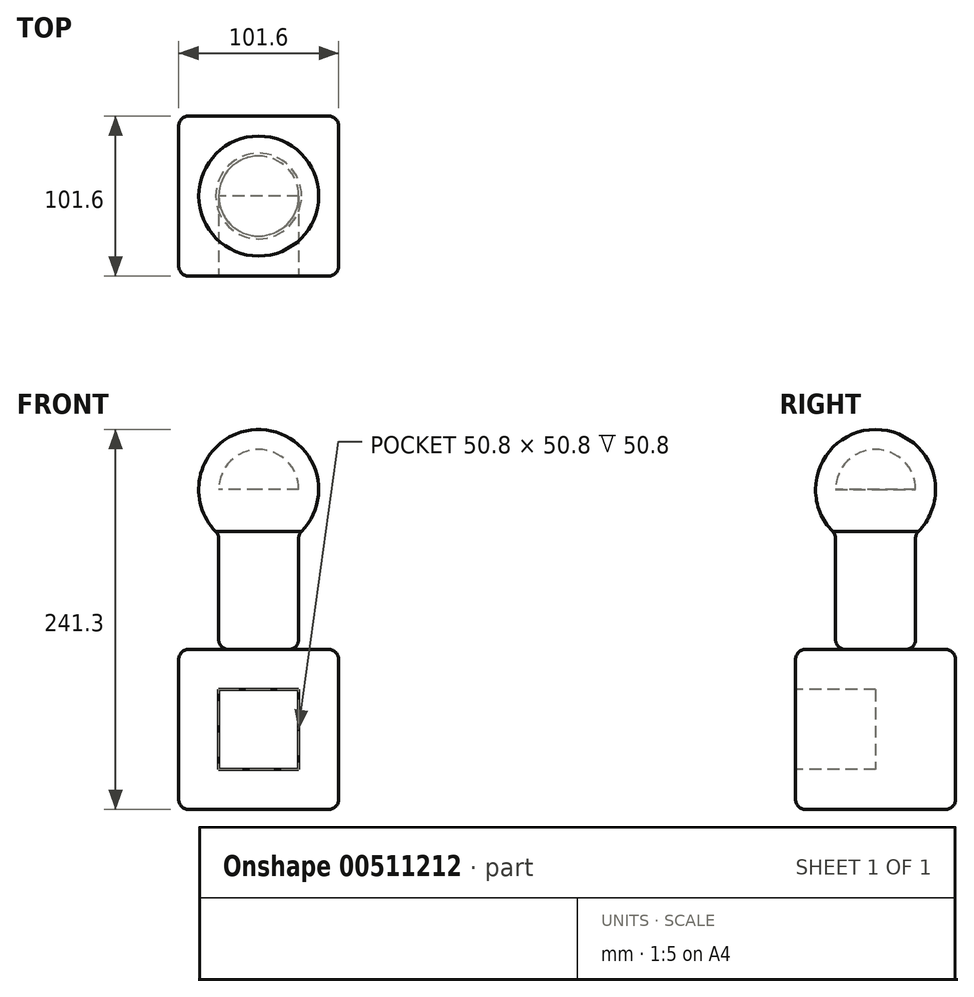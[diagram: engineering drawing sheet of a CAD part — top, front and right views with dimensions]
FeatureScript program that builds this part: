
annotation { "Feature Type Name" : "Feature", "Feature Type Description" : "" }
export const myFeature = defineFeature(function(context is Context, id is Id, definition is map)
    precondition{}
    {
        {
            var Q0;
            Q0=qCreatedBy(makeId("Top.planeOp"),FACE);
            var sketch = newSketch(context, id + "F0", { "sketchPlane" : qUnion([Q0])});
            skLineSegment(sketch, "E0.bottom", {"start": v(50.8, 50.8) * mm, "end": v(-50.8, 50.8) * mm});
            skLineSegment(sketch, "E0.top", {"start": v(50.8, -50.8) * mm, "end": v(-50.8, -50.8) * mm});
            skLineSegment(sketch, "E0.left", {"start": v(50.8, 50.8) * mm, "end": v(50.8, -50.8) * mm});
            skLineSegment(sketch, "E0.right", {"start": v(-50.8, 50.8) * mm, "end": v(-50.8, -50.8) * mm});
            skPoint(sketch, "E0.middle", {"position": v(0, 0) * mm});
            skSolve(sketch);
        }
        {
            var Q0;
            Q0=makeQuery(id+"F0.imprint","IMPRINT",FACE,{"disambiguationData":[TD([[makeQuery(id+"F0.imprint","IMPRINT",EDGE,{"derivedFrom":sQuery(id+"F0.wireOp",EDGE,"E0.bottom")}),1.0]])]});
            extrude(context, id + "F1", {"entities" : qUnion([Q0]), "depth" : 101.6 * mm});
        }
        {
            var Q0;
            Q0=makeQuery(id+"F1.opExtrude","CAP_FACE",FACE,{"disambiguationData":[OSD([sQuery(id+"F0.wireOp",EDGE,"E0.bottom"),sQuery(id+"F0.wireOp",EDGE,"E0.top"),sQuery(id+"F0.wireOp",EDGE,"E0.left"),sQuery(id+"F0.wireOp",EDGE,"E0.right")])],"isStart":false});
            var sketch = newSketch(context, id + "F2", { "sketchPlane" : qUnion([Q0])});
            skCircle(sketch, "E1", {"center": v(0, 0) * mm, "radius": 25.4 * mm});
            skSolve(sketch);
        }
        {
            var Q0;
            Q0=makeQuery(id+"F2.imprint","IMPRINT",FACE,{"disambiguationData":[TD([[makeQuery(id+"F2.imprint","IMPRINT",EDGE,{"derivedFrom":sQuery(id+"F2.wireOp",EDGE,"E1")}),1.0]])]});
            extrude(context, id + "F3", {"entities" : qUnion([Q0]), "depth" : 101.6 * mm});
        }
        {
            var Q0;
            Q0=makeQuery(id+"F3.opExtrude","CAP_FACE",FACE,{"disambiguationData":[OSD([sQuery(id+"F2.wireOp",EDGE,"E1")])],"isStart":false});
            var sketch = newSketch(context, id + "F4", { "sketchPlane" : qUnion([Q0])});
            skArc(sketch, "E2", {"start": v(0, -38.1) * mm, "mid": v(38.1, 0) * mm, "end": v(0, 38.1) * mm});
            skLineSegment(sketch, "E3", {"start": v(0, 38.1) * mm, "end": v(0, -38.1) * mm});
            skSolve(sketch);
        }
        {
            var Q0;
            {var subQ0=sQuery(id+"F4.wireOp",EDGE,"E2");Q0=makeQuery(id+"F4.imprint","IMPRINT",FACE,{"disambiguationData":[TD([[makeQuery(id+"F4.imprint","IMPRINT",EDGE,{"derivedFrom":subQ0}),1.0]])]});}
            var Q1;
            Q1=sQuery(id+"F4.wireOp",EDGE,"E3");
            revolve(context, id + "F5", {"operationType" : NewBodyOperationType.ADD, "entities" : qUnion([Q0]), "axis" : qUnion([Q1]), "revolveType" : RevolveType.FULL});
        }
        {
            var Q0;
            Q0=makeQuery(id+"F1.opExtrude","SWEPT_FACE",FACE,{"disambiguationData":[OSD([sQuery(id+"F0.wireOp",EDGE,"E0.top")])]});
            var sketch = newSketch(context, id + "F6", { "sketchPlane" : qUnion([Q0])});
            skLineSegment(sketch, "E4.bottom", {"start": v(25.4, 76.2) * mm, "end": v(-25.4, 76.2) * mm});
            skLineSegment(sketch, "E4.top", {"start": v(25.4, 25.4) * mm, "end": v(-25.4, 25.4) * mm});
            skLineSegment(sketch, "E4.left", {"start": v(25.4, 76.2) * mm, "end": v(25.4, 25.4) * mm});
            skLineSegment(sketch, "E4.right", {"start": v(-25.4, 76.2) * mm, "end": v(-25.4, 25.4) * mm});
            skPoint(sketch, "E4.middle", {"position": v(0, 50.8) * mm});
            skPoint(sketch, "E4.middle.positionSnap0", {"position": v(50.8, 50.8) * mm});
            skPoint(sketch, "E4.centerSnap0", {"position": v(50.8, 50.8) * mm});
            skSolve(sketch);
        }
        {
            var Q0;
            Q0=makeQuery(id+"F6.imprint","IMPRINT",FACE,{"disambiguationData":[TD([[makeQuery(id+"F6.imprint","IMPRINT",EDGE,{"derivedFrom":sQuery(id+"F6.wireOp",EDGE,"E4.bottom")}),1.0]])]});
            extrude(context, id + "F7", {"entities" : qUnion([Q0]), "operationType" : NewBodyOperationType.REMOVE, "oppositeDirection" : true, "depth" : 50.8 * mm});
        }
        {
            var Q0;
            Q0=makeQuery(id+"F1.opExtrude","SWEPT_FACE",FACE,{"disambiguationData":[OSD([sQuery(id+"F0.wireOp",EDGE,"E0.left")])]});
            var Q1;
            Q1=makeQuery(id+"F1.opExtrude","CAP_FACE",FACE,{"disambiguationData":[OSD([sQuery(id+"F0.wireOp",EDGE,"E0.bottom"),sQuery(id+"F0.wireOp",EDGE,"E0.top"),sQuery(id+"F0.wireOp",EDGE,"E0.left"),sQuery(id+"F0.wireOp",EDGE,"E0.right")])],"isStart":false});
            var Q2;
            Q2=makeQuery(id+"F1.opExtrude","SWEPT_FACE",FACE,{"disambiguationData":[OSD([sQuery(id+"F0.wireOp",EDGE,"E0.right")])]});
            var Q3;
            Q3=makeQuery(id+"F1.opExtrude","SWEPT_FACE",FACE,{"disambiguationData":[OSD([sQuery(id+"F0.wireOp",EDGE,"E0.bottom")])]});
            var Q4;
            Q4=makeQuery(id+"F1.opExtrude","CAP_FACE",FACE,{"disambiguationData":[OSD([sQuery(id+"F0.wireOp",EDGE,"E0.bottom"),sQuery(id+"F0.wireOp",EDGE,"E0.top"),sQuery(id+"F0.wireOp",EDGE,"E0.left"),sQuery(id+"F0.wireOp",EDGE,"E0.right")])],"isStart":true});
            var Q5;
            Q5=makeQuery(id+"F3.opExtrude","CAP_EDGE",EDGE,{"disambiguationData":[OSD([sQuery(id+"F2.wireOp",EDGE,"E1")])],"isStart":true});
            var Q6;
            Q6=makeQuery(id+"F5.boolean.opBoolean","INTERSECT",EDGE,{"derivedFrom":[makeQuery(id+"F3.opExtrude","SWEPT_FACE",FACE,{"disambiguationData":[OSD([sQuery(id+"F2.wireOp",EDGE,"E1")])]}),makeQuery(id+"F5.opRevolve","SWEPT_FACE",FACE,{"disambiguationData":[OSD([sQuery(id+"F4.wireOp",EDGE,"E2")])]})]});
            fillet(context, id + "F8", {"entities" : qUnion([Q0, Q1, Q2, Q3, Q4, Q5, Q6]), "radius" : 6.35 * mm, "tangentPropagation" : true, "allowEdgeOverflow" : false});
        }
    });
